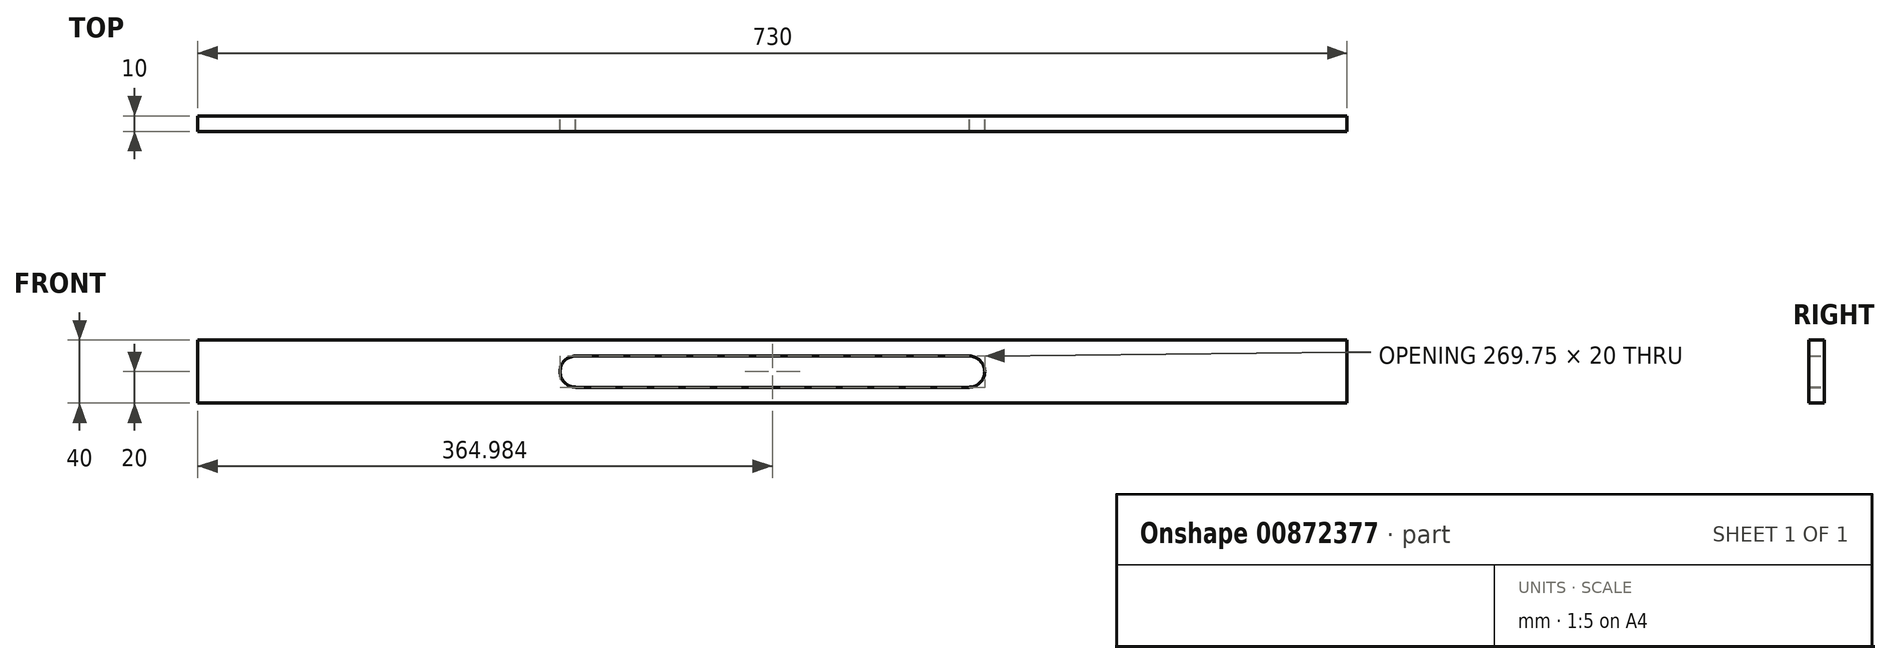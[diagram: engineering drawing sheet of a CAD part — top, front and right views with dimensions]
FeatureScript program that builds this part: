
annotation { "Feature Type Name" : "Feature", "Feature Type Description" : "" }
export const myFeature = defineFeature(function(context is Context, id is Id, definition is map)
    precondition{}
    {
        {
            var Q0;
            Q0=qCreatedBy(makeId("Front.planeOp"),FACE);
            var sketch = newSketch(context, id + "F0", { "sketchPlane" : qUnion([Q0])});
            skLineSegment(sketch, "E0.bottom", {"start": v(365, -20) * mm, "end": v(-365, -20) * mm});
            skLineSegment(sketch, "E0.top", {"start": v(365, 20) * mm, "end": v(-365, 20) * mm});
            skLineSegment(sketch, "E0.left", {"start": v(365, -20) * mm, "end": v(365, 20) * mm});
            skLineSegment(sketch, "E0.right", {"start": v(-365, -20) * mm, "end": v(-365, 20) * mm});
            skPoint(sketch, "E0.middle", {"position": v(0, 0) * mm});
            skLineSegment(sketch, "E1", {"start": v(-365, 10) * mm, "end": v(365, 10) * mm});
            skLineSegment(sketch, "E2", {"start": v(365, 10) * mm, "end": v(365, -10) * mm});
            skLineSegment(sketch, "E3", {"start": v(365, -10) * mm, "end": v(-365, -10) * mm});
            skLineSegment(sketch, "E4", {"start": v(-125, 10) * mm, "end": v(-125, -10) * mm});
            skLineSegment(sketch, "E5", {"start": v(125, 10) * mm, "end": v(125, -10) * mm});
            skCircle(sketch, "E6", {"center": v(-125, 0) * mm, "radius": 9.9 * mm});
            skCircle(sketch, "E7", {"center": v(125, 0) * mm, "radius": 9.86 * mm});
            skSolve(sketch);
        }
        {
            var Q0;
            Q0=qSketchRegion(id+"F0",true);
            extrude(context, id + "F1", {"entities" : qUnion([Q0]), "depth" : 10 * mm, "offsetDistance" : 25 * mm});
        }
    });
